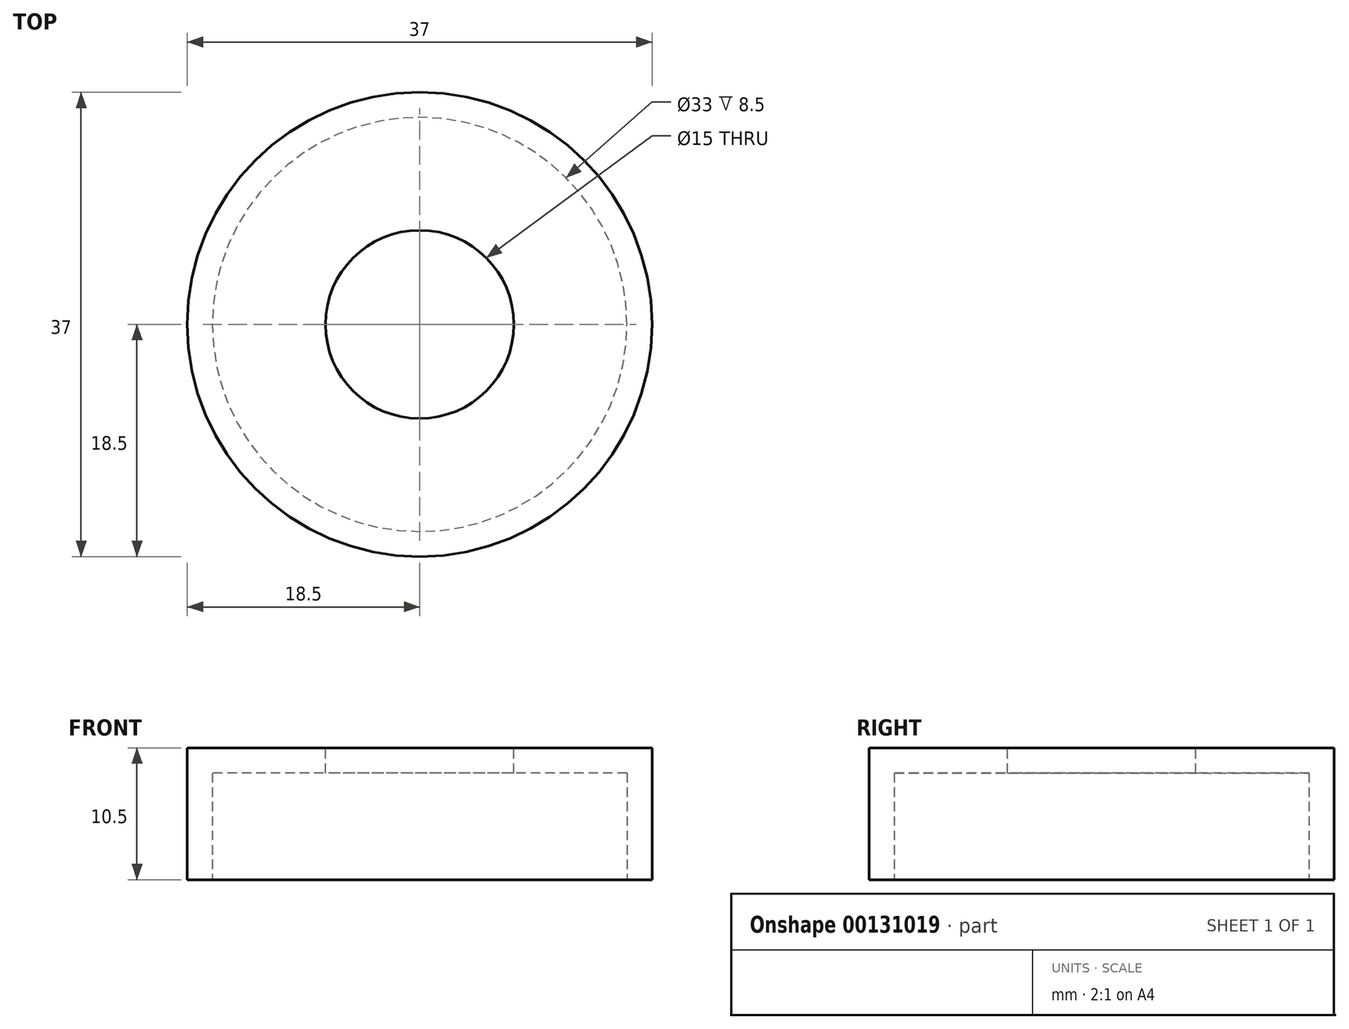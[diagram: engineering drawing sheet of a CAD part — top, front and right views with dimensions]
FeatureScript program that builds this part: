
annotation { "Feature Type Name" : "Feature", "Feature Type Description" : "" }
export const myFeature = defineFeature(function(context is Context, id is Id, definition is map)
    precondition{}
    {
        {
            var Q0;
            Q0=qCreatedBy(makeId("Top.planeOp"),FACE);
            var sketch = newSketch(context, id + "F0", { "sketchPlane" : qUnion([Q0])});
            skCircle(sketch, "E0.0", {"center": v(0, 0) * mm, "radius": 18.5 * mm});
            skSolve(sketch);
        }
        {
            var Q0;
            Q0=makeQuery(id+"F0.imprint","IMPRINT",FACE,{"disambiguationData":[TD([[makeQuery(id+"F0.imprint","IMPRINT",EDGE,{"derivedFrom":sQuery(id+"F0.wireOp",EDGE,"E0.0")}),1.0]])]});
            extrude(context, id + "F1", {"entities" : qUnion([Q0]), "depth" : 10.5 * mm});
        }
        {
            var Q0;
            Q0=makeQuery(id+"F1.opExtrude","CAP_FACE",FACE,{"disambiguationData":[OSD([sQuery(id+"F0.wireOp",EDGE,"E0.0")])],"isStart":true});
            shell(context, id + "F2", {"entities" : qUnion([Q0]), "thickness" : 2 * mm});
        }
        {
            var Q0;
            Q0=makeQuery(id+"F1.opExtrude","CAP_FACE",FACE,{"disambiguationData":[OSD([sQuery(id+"F0.wireOp",EDGE,"E0.0")])],"isStart":false});
            var sketch = newSketch(context, id + "F3", { "sketchPlane" : qUnion([Q0])});
            skCircle(sketch, "E1", {"center": v(0, 0) * mm, "radius": 7.5 * mm});
            skSolve(sketch);
        }
        {
            var Q0;
            Q0 = qSketchRegion(id + "F3", true);
            var Q1;
            {var subQ0=sQuery(id+"F0.wireOp",EDGE,"E0.0");Q1=makeQuery(id+"F2.opShell","OFFSET_FACE",FACE,{"disambiguationData":[OSD([subQ0]),TDD([makeQuery(id+"F1.opExtrude","CAP_FACE",FACE,{"disambiguationData":[OSD([subQ0])],"isStart":false})])]});}
            extrude(context, id + "F4", {"entities" : qUnion([Q0]), "operationType" : NewBodyOperationType.REMOVE, "endBound" : BoundingType.UP_TO_SURFACE, "oppositeDirection" : true, "endBoundEntityFace" : qUnion([Q1]), "depth" : 25 * mm});
        }
    });
